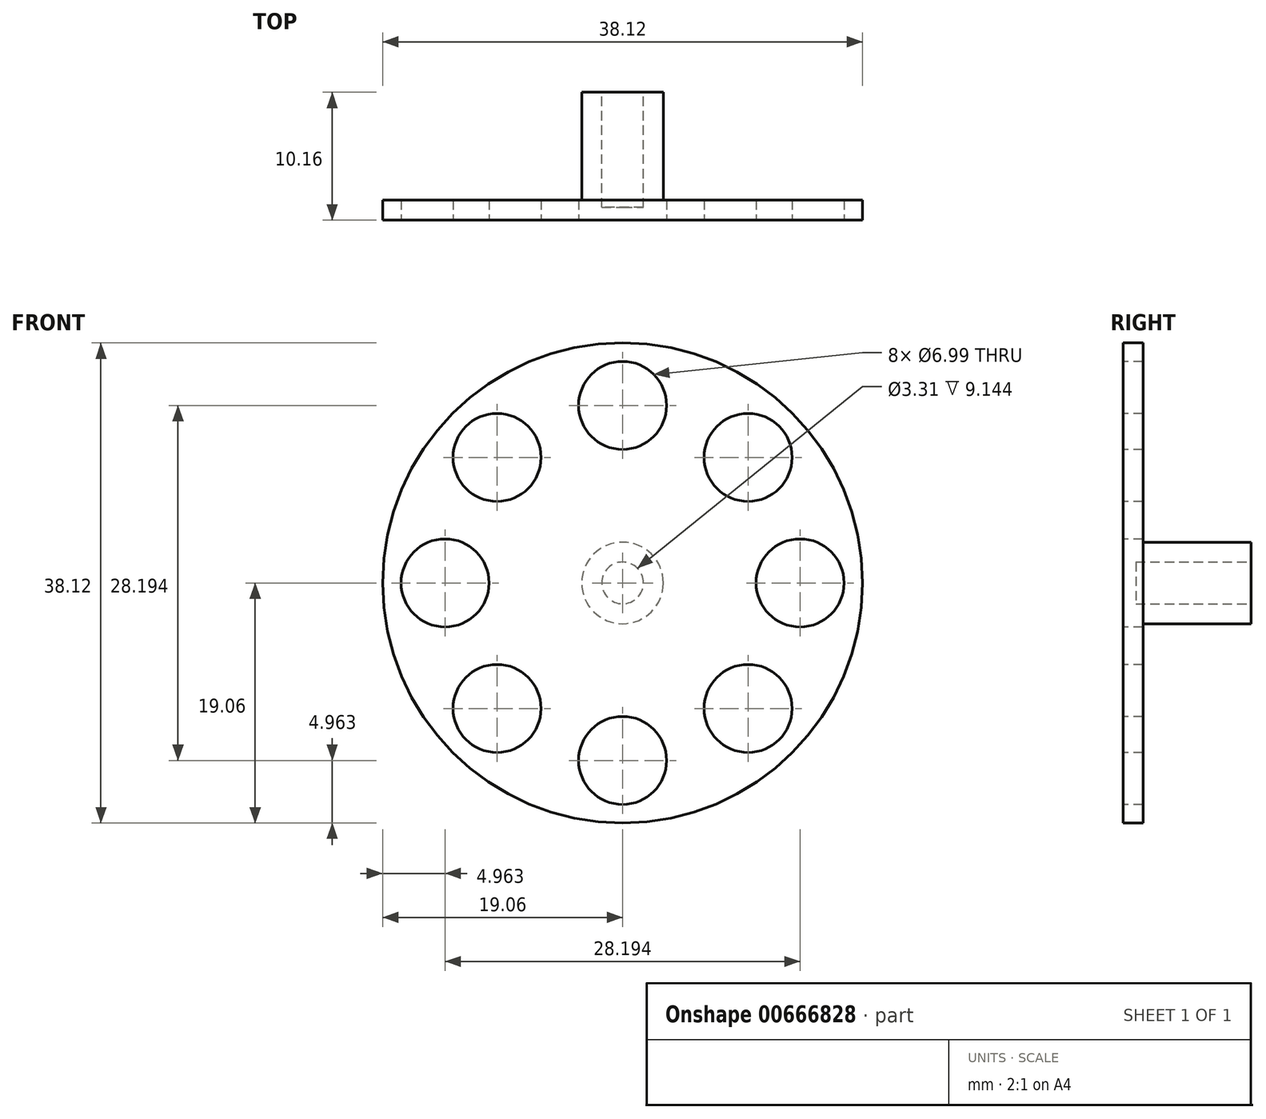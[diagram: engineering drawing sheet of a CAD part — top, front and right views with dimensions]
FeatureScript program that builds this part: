
annotation { "Feature Type Name" : "Feature", "Feature Type Description" : "" }
export const myFeature = defineFeature(function(context is Context, id is Id, definition is map)
    precondition{}
    {
        {
            var Q0;
            Q0=qCreatedBy(makeId("Front.planeOp"),FACE);
            var sketch = newSketch(context, id + "F0", { "sketchPlane" : qUnion([Q0])});
            skCircle(sketch, "E0", {"center": v(0, 0) * mm, "radius": 19.06 * mm});
            skSolve(sketch);
        }
        {
            var Q0;
            Q0 = qSketchRegion(id + "F0", true);
            extrude(context, id + "F1", {"entities" : qUnion([Q0]), "oppositeDirection" : true, "depth" : 1.59 * mm, "offsetDistance" : 25.4 * mm});
        }
        {
            var Q0;
            Q0=makeQuery(id+"F1.opExtrude","CAP_FACE",FACE,{"disambiguationData":[OSD([sQuery(id+"F0.wireOp",EDGE,"E0")])],"isStart":true});
            var sketch = newSketch(context, id + "F2", { "sketchPlane" : qUnion([Q0])});
            skCircle(sketch, "E1", {"center": v(0, 14.1) * mm, "radius": 3.5 * mm});
            skCircle(sketch, "E2.1.0", {"center": v(-9.97, 9.97) * mm, "radius": 3.5 * mm});
            skCircle(sketch, "E2.2.0", {"center": v(-14.1, 0) * mm, "radius": 3.5 * mm});
            skCircle(sketch, "E2.3.0", {"center": v(-9.97, -9.97) * mm, "radius": 3.5 * mm});
            skCircle(sketch, "E2.4.0", {"center": v(0, -14.1) * mm, "radius": 3.5 * mm});
            skCircle(sketch, "E2.5.0", {"center": v(9.97, -9.97) * mm, "radius": 3.5 * mm});
            skCircle(sketch, "E2.6.0", {"center": v(14.1, 0) * mm, "radius": 3.5 * mm});
            skCircle(sketch, "E2.7.0", {"center": v(9.97, 9.97) * mm, "radius": 3.5 * mm});
            skPoint(sketch, "E2.center", {"position": v(0, 0) * mm});
            skSolve(sketch);
        }
        {
            var Q0;
            Q0 = qSketchRegion(id + "F2", true);
            extrude(context, id + "F3", {"entities" : qUnion([Q0]), "operationType" : NewBodyOperationType.REMOVE, "oppositeDirection" : true, "depth" : 21.08 * mm, "offsetDistance" : 25.4 * mm});
        }
        {
            var Q0;
            Q0=qCreatedBy(makeId("Front.planeOp"),FACE);
            var sketch = newSketch(context, id + "F4", { "sketchPlane" : qUnion([Q0])});
            skCircle(sketch, "E3", {"center": v(0, 0) * mm, "radius": 3.24 * mm});
            skSolve(sketch);
        }
        {
            var Q0;
            Q0 = qSketchRegion(id + "F4", true);
            extrude(context, id + "F5", {"entities" : qUnion([Q0]), "operationType" : NewBodyOperationType.ADD, "oppositeDirection" : true, "depth" : 10.16 * mm, "offsetDistance" : 25.4 * mm});
        }
        {
            var Q0;
            Q0=makeQuery(id+"F5.opExtrude","CAP_FACE",FACE,{"disambiguationData":[OSD([sQuery(id+"F4.wireOp",EDGE,"E3")])],"isStart":false});
            var sketch = newSketch(context, id + "F6", { "sketchPlane" : qUnion([Q0])});
            skCircle(sketch, "E4", {"center": v(0, 0) * mm, "radius": 1.66 * mm});
            skSolve(sketch);
        }
        {
            var Q0;
            Q0=makeQuery(id+"F6.imprint","IMPRINT",FACE,{"disambiguationData":[TD([[makeQuery(id+"F6.imprint","IMPRINT",EDGE,{"derivedFrom":sQuery(id+"F6.wireOp",EDGE,"E4")}),1.0]])]});
            extrude(context, id + "F7", {"entities" : qUnion([Q0]), "operationType" : NewBodyOperationType.REMOVE, "oppositeDirection" : true, "depth" : 9.14 * mm, "offsetDistance" : 25.4 * mm});
        }
    });
